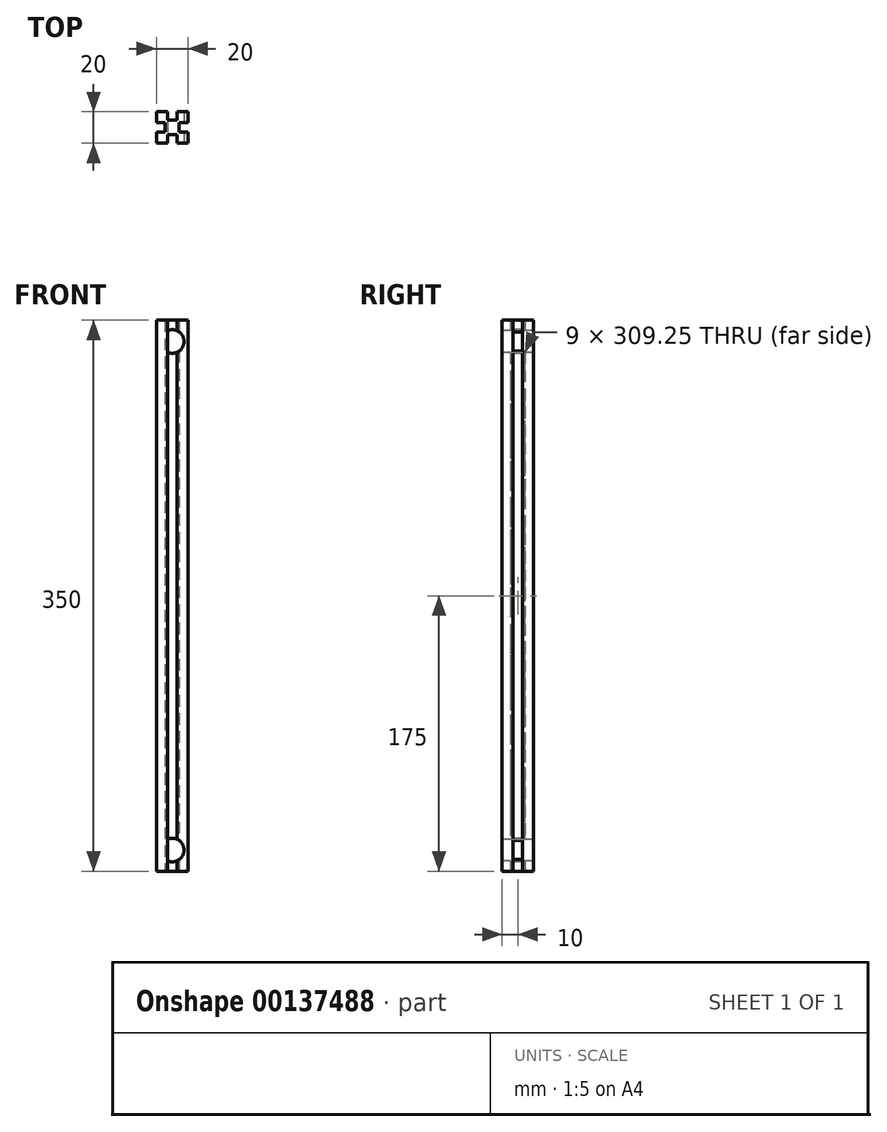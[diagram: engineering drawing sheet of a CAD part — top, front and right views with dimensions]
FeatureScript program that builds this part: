
annotation { "Feature Type Name" : "Feature", "Feature Type Description" : "" }
export const myFeature = defineFeature(function(context is Context, id is Id, definition is map)
    precondition{}
    {
        {
            var Q0;
            Q0=qCreatedBy(makeId("Top.planeOp"),FACE);
            var sketch = newSketch(context, id + "F0", { "sketchPlane" : qUnion([Q0])});
            skLineSegment(sketch, "E0.bottom", {"start": v(0, 0) * mm, "end": v(20, 0) * mm});
            skLineSegment(sketch, "E0.top", {"start": v(0, 20) * mm, "end": v(20, 20) * mm});
            skLineSegment(sketch, "E0.left", {"start": v(0, 0) * mm, "end": v(0, 20) * mm});
            skLineSegment(sketch, "E0.right", {"start": v(20, 0) * mm, "end": v(20, 20) * mm});
            skLineSegment(sketch, "E1.bottom", {"start": v(7, 20) * mm, "end": v(13, 20) * mm});
            skLineSegment(sketch, "E1.top", {"start": v(7, 14.5) * mm, "end": v(13, 14.5) * mm});
            skLineSegment(sketch, "E1.left", {"start": v(7, 20) * mm, "end": v(7, 14.5) * mm});
            skLineSegment(sketch, "E1.right", {"start": v(13, 20) * mm, "end": v(13, 14.5) * mm});
            skLineSegment(sketch, "E2.bottom", {"start": v(20, 13) * mm, "end": v(14.5, 13) * mm});
            skLineSegment(sketch, "E2.top", {"start": v(20, 7) * mm, "end": v(14.5, 7) * mm});
            skLineSegment(sketch, "E2.left", {"start": v(20, 13) * mm, "end": v(20, 7) * mm});
            skLineSegment(sketch, "E2.right", {"start": v(14.5, 13) * mm, "end": v(14.5, 7) * mm});
            skLineSegment(sketch, "E3.bottom", {"start": v(13, 0) * mm, "end": v(7, 0) * mm});
            skLineSegment(sketch, "E3.top", {"start": v(13, 5.5) * mm, "end": v(7, 5.5) * mm});
            skLineSegment(sketch, "E3.left", {"start": v(13, 0) * mm, "end": v(13, 5.5) * mm});
            skLineSegment(sketch, "E3.right", {"start": v(7, 0) * mm, "end": v(7, 5.5) * mm});
            skLineSegment(sketch, "E4.bottom", {"start": v(0, 7) * mm, "end": v(5.5, 7) * mm});
            skLineSegment(sketch, "E4.top", {"start": v(0, 13) * mm, "end": v(5.5, 13) * mm});
            skLineSegment(sketch, "E4.left", {"start": v(0, 7) * mm, "end": v(0, 13) * mm});
            skLineSegment(sketch, "E4.right", {"start": v(5.5, 7) * mm, "end": v(5.5, 13) * mm});
            skSolve(sketch);
        }
        {
            var Q0;
            Q0=makeQuery(id+"F0.imprint","IMPRINT",FACE,{"disambiguationData":[TD([[makeQuery(id+"F0.imprint","IMPRINT",EDGE,{"derivedFrom":sQuery(id+"F0.wireOp",EDGE,"E1.top")}),-1.0]])]});
            extrude(context, id + "F1", {"entities" : qUnion([Q0]), "depth" : 350 * mm});
        }
        {
            var Q0;
            {var subQ0=sQuery(id+"F0.wireOp",EDGE,"E0.bottom");Q0=makeQuery(id+"F1.opExtrude","SWEPT_FACE",FACE,{"disambiguationData":[OSD([subQ0]),TDD([makeQuery(id+"F0.imprint","IMPRINT",EDGE,{"disambiguationData":[TD([[makeQuery(id+"F0.imprint","INTERSECT",VERTEX,{"derivedFrom":[subQ0,sQuery(id+"F0.wireOp",EDGE,"E0.left")]}),-1.0]])],"derivedFrom":subQ0})])]});}
            var sketch = newSketch(context, id + "F2", { "sketchPlane" : qUnion([Q0])});
            skCircle(sketch, "E5", {"center": v(10, 336.5) * mm, "radius": 7.5 * mm});
            skCircle(sketch, "E6", {"center": v(10, 13.5) * mm, "radius": 7.5 * mm});
            skCircle(sketch, "E7", {"center": v(10, 318.5) * mm, "radius": 2 * mm});
            skCircle(sketch, "E8", {"center": v(10, 31.5) * mm, "radius": 2 * mm});
            skLineSegment(sketch, "E9", {"start": v(10, 318.5) * mm, "end": v(10, 329) * mm});
            skLineSegment(sketch, "E10", {"start": v(10, 31.5) * mm, "end": v(10, 21) * mm});
            skSolve(sketch);
        }
        {
            var Q0;
            {var subQ0=sQuery(id+"F2.wireOp",EDGE,"E5");var subQ1=makeQuery(id+"F2.imprint","IMPRINT",VERTEX,{"derivedFrom":subQ0});Q0=makeQuery(id+"F2.imprint","IMPRINT",FACE,{"disambiguationData":[TD([[makeQuery(id+"F2.imprint","IMPRINT",EDGE,{"disambiguationData":[TD([[subQ1,1.0]])],"derivedFrom":subQ0}),1.0]])]});}
            var Q1;
            {var subQ0=sQuery(id+"F2.wireOp",EDGE,"E6");var subQ1=makeQuery(id+"F2.imprint","IMPRINT",VERTEX,{"derivedFrom":subQ0});Q1=makeQuery(id+"F2.imprint","IMPRINT",FACE,{"disambiguationData":[TD([[makeQuery(id+"F2.imprint","IMPRINT",EDGE,{"disambiguationData":[TD([[subQ1,-1.0]])],"derivedFrom":subQ0}),1.0]])]});}
            var Q2;
            {var subQ0=sQuery(id+"F2.wireOp",EDGE,"E5");var subQ1=makeQuery(id+"F1.opExtrude","SWEPT_EDGE",EDGE,{"disambiguationData":[OSD([sQuery(id+"F0.wireOp",EDGE,"E0.bottom"),sQuery(id+"F0.wireOp",EDGE,"E3.bottom"),sQuery(id+"F0.wireOp",EDGE,"E3.right")])]});var subQ2=makeQuery(id+"F2.imprint","INTERSECT",VERTEX,{"disambiguationData":[OD(0.0)],"derivedFrom":[subQ1,subQ0]});Q2=makeQuery(id+"F2.imprint","IMPRINT",FACE,{"disambiguationData":[TD([[makeQuery(id+"F2.imprint","IMPRINT",EDGE,{"disambiguationData":[TD([[subQ2,1.0]])],"derivedFrom":subQ0}),1.0]])]});}
            var Q3;
            {var subQ0=sQuery(id+"F2.wireOp",EDGE,"E6");var subQ1=makeQuery(id+"F1.opExtrude","SWEPT_EDGE",EDGE,{"disambiguationData":[OSD([sQuery(id+"F0.wireOp",EDGE,"E0.bottom"),sQuery(id+"F0.wireOp",EDGE,"E3.bottom"),sQuery(id+"F0.wireOp",EDGE,"E3.right")])]});var subQ2=makeQuery(id+"F2.imprint","INTERSECT",VERTEX,{"disambiguationData":[OD(0.0)],"derivedFrom":[subQ1,subQ0]});Q3=makeQuery(id+"F2.imprint","IMPRINT",FACE,{"disambiguationData":[TD([[makeQuery(id+"F2.imprint","IMPRINT",EDGE,{"disambiguationData":[TD([[subQ2,-1.0]])],"derivedFrom":subQ0}),1.0]])]});}
            extrude(context, id + "F3", {"entities" : qUnion([Q0, Q1, Q2, Q3]), "operationType" : NewBodyOperationType.REMOVE, "oppositeDirection" : true, "depth" : 25 * mm});
        }
    });
